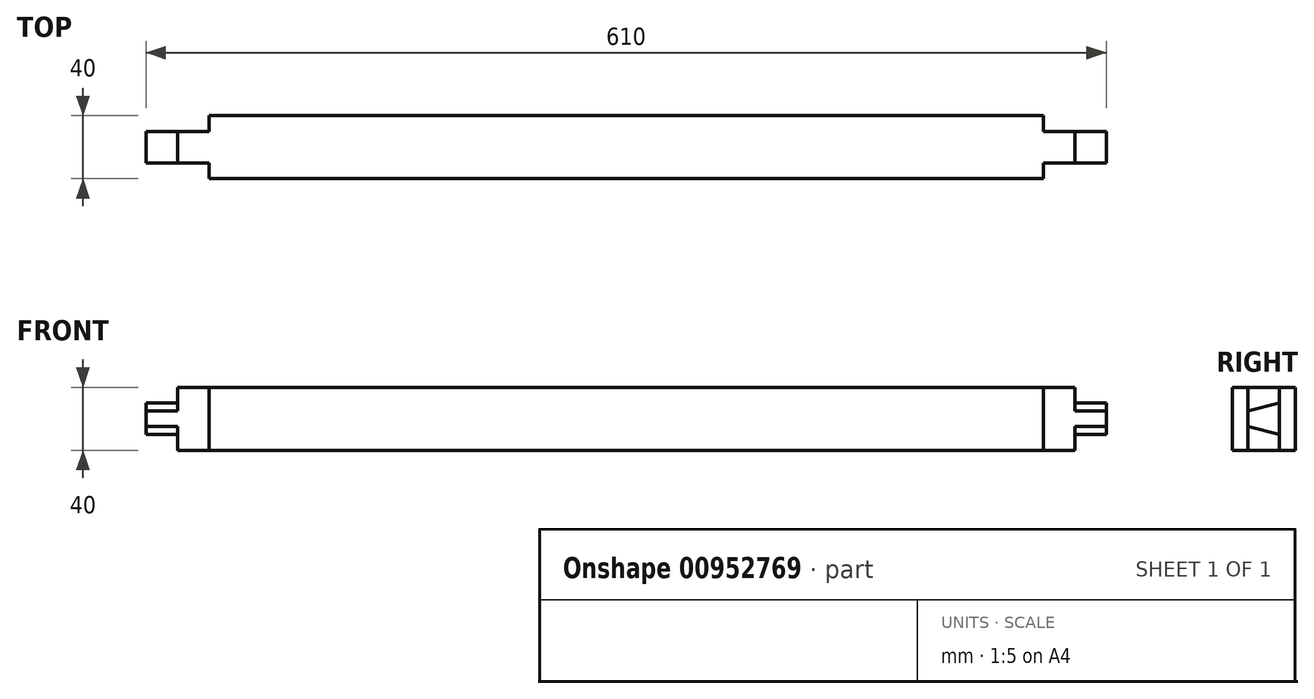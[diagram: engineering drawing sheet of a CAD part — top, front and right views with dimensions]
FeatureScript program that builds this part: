
annotation { "Feature Type Name" : "Feature", "Feature Type Description" : "" }
export const myFeature = defineFeature(function(context is Context, id is Id, definition is map)
    precondition{}
    {
        {
            var Q0;
            Q0=qCreatedBy(makeId("Right.planeOp"),FACE);
            var sketch = newSketch(context, id + "F0", { "sketchPlane" : qUnion([Q0])});
            skLineSegment(sketch, "E0.bottom", {"start": v(-23.23, 28.19) * mm, "end": v(16.77, 28.19) * mm});
            skLineSegment(sketch, "E0.top", {"start": v(-23.23, -11.81) * mm, "end": v(16.77, -11.81) * mm});
            skLineSegment(sketch, "E0.left", {"start": v(-23.23, 28.19) * mm, "end": v(-23.23, -11.81) * mm});
            skLineSegment(sketch, "E0.right", {"start": v(16.77, 28.19) * mm, "end": v(16.77, -11.81) * mm});
            skSolve(sketch);
        }
        {
            var Q0;
            Q0=makeQuery(id+"F0.imprint","IMPRINT",FACE,{"disambiguationData":[TD([[makeQuery(id+"F0.imprint","IMPRINT",EDGE,{"derivedFrom":sQuery(id+"F0.wireOp",EDGE,"E0.bottom")}),-1.0]])]});
            extrude(context, id + "F1", {"entities" : qUnion([Q0]), "depth" : 265 * mm, "offsetDistance" : 25 * mm});
        }
        {
            var Q0;
            Q0=makeQuery(id+"F1.opExtrude","CAP_FACE",FACE,{"disambiguationData":[OSD([sQuery(id+"F0.wireOp",EDGE,"E0.bottom"),sQuery(id+"F0.wireOp",EDGE,"E0.top"),sQuery(id+"F0.wireOp",EDGE,"E0.left"),sQuery(id+"F0.wireOp",EDGE,"E0.right")])],"isStart":false});
            var sketch = newSketch(context, id + "F2", { "sketchPlane" : qUnion([Q0])});
            skLineSegment(sketch, "E1.bottom", {"start": v(-13.23, 28.19) * mm, "end": v(6.77, 28.19) * mm});
            skLineSegment(sketch, "E1.top", {"start": v(-13.23, -11.81) * mm, "end": v(6.77, -11.81) * mm});
            skLineSegment(sketch, "E1.left", {"start": v(-13.23, 28.19) * mm, "end": v(-13.23, -11.81) * mm});
            skLineSegment(sketch, "E1.right", {"start": v(6.77, 28.19) * mm, "end": v(6.77, -11.81) * mm});
            skSolve(sketch);
        }
        {
            var Q0;
            Q0=makeQuery(id+"F2.imprint","IMPRINT",FACE,{"disambiguationData":[TD([[makeQuery(id+"F2.imprint","IMPRINT",EDGE,{"derivedFrom":sQuery(id+"F2.wireOp",EDGE,"E1.bottom")}),-1.0]])]});
            extrude(context, id + "F3", {"entities" : qUnion([Q0]), "operationType" : NewBodyOperationType.ADD, "depth" : 40 * mm, "offsetDistance" : 25 * mm});
        }
        {
            var Q0;
            Q0=makeQuery(id+"F3.opExtrude","CAP_FACE",FACE,{"disambiguationData":[OSD([sQuery(id+"F2.wireOp",EDGE,"E1.bottom"),sQuery(id+"F2.wireOp",EDGE,"E1.top"),sQuery(id+"F2.wireOp",EDGE,"E1.left"),sQuery(id+"F2.wireOp",EDGE,"E1.right")])],"isStart":false});
            var sketch = newSketch(context, id + "F4", { "sketchPlane" : qUnion([Q0])});
            skLineSegment(sketch, "E2", {"start": v(-13.23, 13.19) * mm, "end": v(6.77, 18.19) * mm});
            skLineSegment(sketch, "E3", {"start": v(6.77, 18.19) * mm, "end": v(6.77, -1.81) * mm});
            skLineSegment(sketch, "E4", {"start": v(6.77, -1.81) * mm, "end": v(-13.23, 3.19) * mm});
            skSolve(sketch);
        }
        {
            var Q0;
            {var subQ0=sQuery(id+"F4.wireOp",EDGE,"E4");Q0=makeQuery(id+"F4.imprint","IMPRINT",FACE,{"disambiguationData":[TD([[makeQuery(id+"F4.imprint","IMPRINT",EDGE,{"derivedFrom":subQ0}),1.0]])]});}
            var Q1;
            {var subQ0=sQuery(id+"F4.wireOp",EDGE,"E2");Q1=makeQuery(id+"F4.imprint","IMPRINT",FACE,{"disambiguationData":[TD([[makeQuery(id+"F4.imprint","IMPRINT",EDGE,{"derivedFrom":subQ0}),1.0]])]});}
            extrude(context, id + "F5", {"entities" : qUnion([Q0, Q1]), "operationType" : NewBodyOperationType.REMOVE, "oppositeDirection" : true, "depth" : 20 * mm, "offsetDistance" : 25 * mm});
        }
        {
            var Q0;
            Q0=makeQuery(id+"F1.opExtrude","SWEPT_BODY",BODY,{"disambiguationData":[OSD([sQuery(id+"F0.wireOp",EDGE,"E0.bottom"),sQuery(id+"F0.wireOp",EDGE,"E0.top"),sQuery(id+"F0.wireOp",EDGE,"E0.left"),sQuery(id+"F0.wireOp",EDGE,"E0.right")])]});
            var Q1;
            Q1=makeQuery(id+"F1.opExtrude","CAP_FACE",FACE,{"disambiguationData":[OSD([sQuery(id+"F0.wireOp",EDGE,"E0.bottom"),sQuery(id+"F0.wireOp",EDGE,"E0.top"),sQuery(id+"F0.wireOp",EDGE,"E0.left"),sQuery(id+"F0.wireOp",EDGE,"E0.right")])],"isStart":true});
            mirror(context, id + "F6", {"operationType" : NewBodyOperationType.ADD, "entities" : qUnion([Q0]), "mirrorPlane" : qUnion([Q1])});
        }
    });
